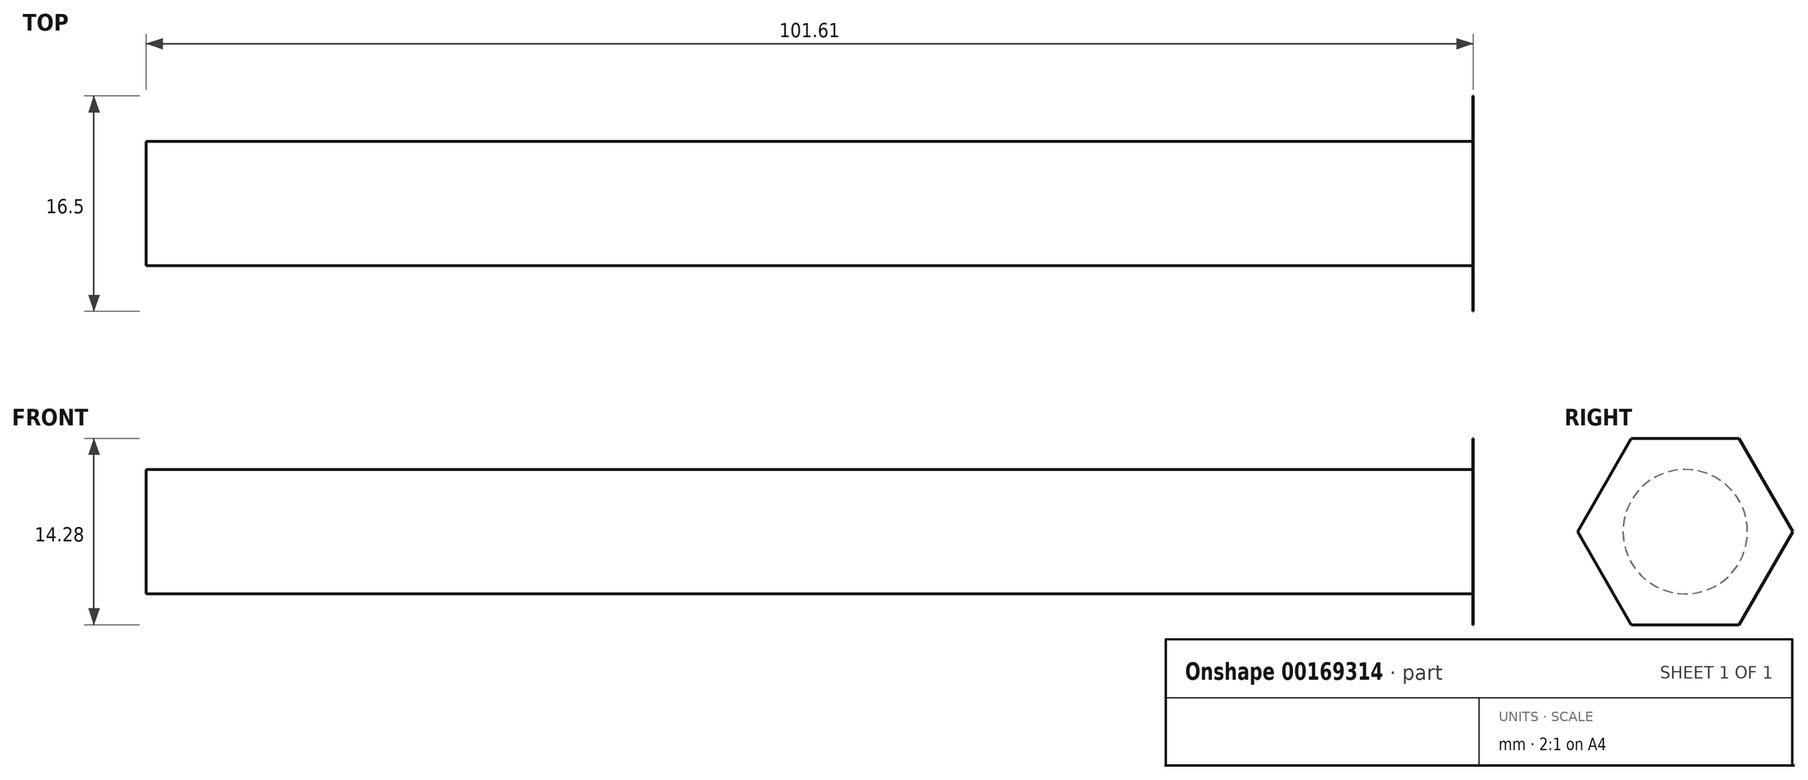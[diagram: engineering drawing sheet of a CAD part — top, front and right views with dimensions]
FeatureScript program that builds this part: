
annotation { "Feature Type Name" : "Feature", "Feature Type Description" : "" }
export const myFeature = defineFeature(function(context is Context, id is Id, definition is map)
    precondition{}
    {
        {
            var Q0;
            Q0=qCreatedBy(makeId("Right.planeOp"),FACE);
            var sketch = newSketch(context, id + "F0", { "sketchPlane" : qUnion([Q0])});
            skCircle(sketch, "E0.cCircle", {"center": v(0, 0) * mm, "radius": 7.14 * mm, "construction": true});
            skLineSegment(sketch, "E0.0", {"start": v(-4.12, 7.14) * mm, "end": v(4.12, 7.14) * mm});
            skLineSegment(sketch, "E0.1", {"start": v(4.12, 7.14) * mm, "end": v(8.25, 0) * mm});
            skLineSegment(sketch, "E0.2", {"start": v(8.25, 0) * mm, "end": v(4.12, -7.14) * mm});
            skLineSegment(sketch, "E0.3", {"start": v(4.12, -7.14) * mm, "end": v(-4.12, -7.14) * mm});
            skLineSegment(sketch, "E0.4", {"start": v(-4.12, -7.14) * mm, "end": v(-8.25, 0) * mm});
            skLineSegment(sketch, "E0.5", {"start": v(-8.25, 0) * mm, "end": v(-4.12, 7.14) * mm});
            skPoint(sketch, "E0.0.midPoint", {"position": v(0, 7.14) * mm});
            skSolve(sketch);
        }
        {
            var Q0;
            Q0=makeQuery(id+"F0.imprint","IMPRINT",FACE,{"disambiguationData":[TD([[makeQuery(id+"F0.imprint","IMPRINT",EDGE,{"derivedFrom":sQuery(id+"F0.wireOp",EDGE,"E0.0")}),-1.0]])]});
            extrude(context, id + "F1", {"entities" : qUnion([Q0]), "depth" : 1 / 101.6 * mm});
        }
        {
            var Q0;
            Q0=qCreatedBy(makeId("Right.planeOp"),FACE);
            var sketch = newSketch(context, id + "F2", { "sketchPlane" : qUnion([Q0])});
            skCircle(sketch, "E1", {"center": v(0, 0) * mm, "radius": 4.76 * mm});
            skSolve(sketch);
        }
        {
            var Q0;
            Q0 = qSketchRegion(id + "F2", true);
            extrude(context, id + "F3", {"entities" : qUnion([Q0]), "operationType" : NewBodyOperationType.ADD, "oppositeDirection" : true, "depth" : 101.6 * mm});
        }
    });
